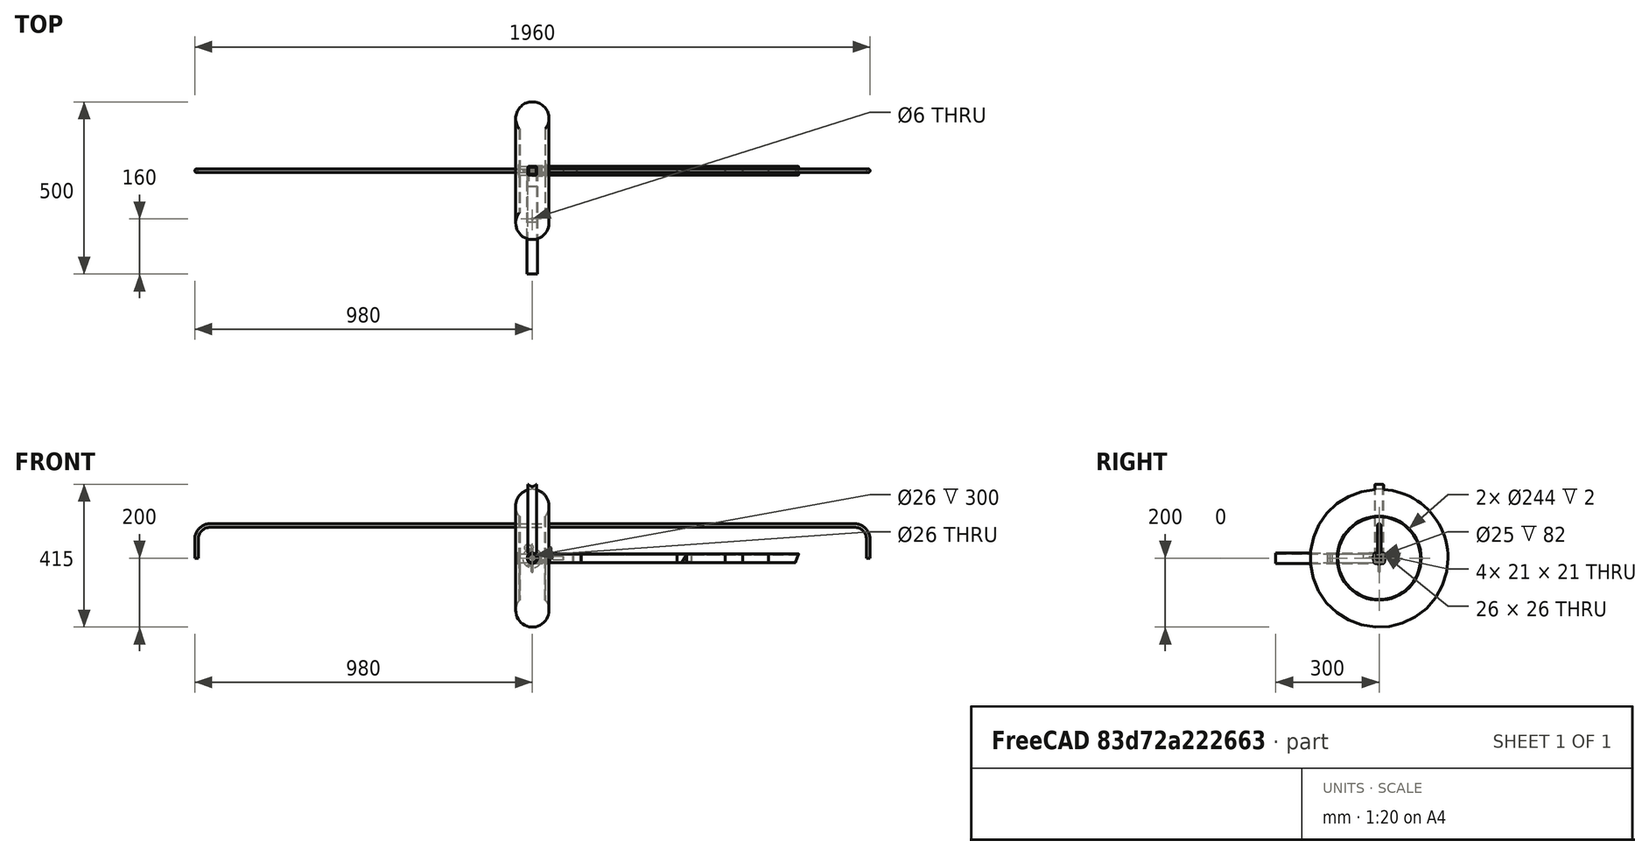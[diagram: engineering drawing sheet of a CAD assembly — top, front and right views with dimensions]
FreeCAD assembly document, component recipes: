
FREECAD ASSEMBLY — COMPONENT RECIPES ("brouetteas4")

This assembly document has 25 components, labeled P0..P24 below (a component is one placed body or linked part). 24 of them carry a construction recipe — the FreeCAD feature program that regenerates the part from scratch, quoted from this document or its linked companion documents; the rest are supplied as boundary geometry only. No exploded tour is included for this assembly.
COMPONENT P0 — recipe-attached ("A1", modeled in this document).
Construction recipe (the document's own serialized feature program — sketch geometry with constraints, then the solid features built on it; lengths are millimeters unless a unit is written):

FEATURE [PartDesign::Body] A1005
  AllowCompound = false
  Origin = -> Origin015
COMPONENT P1 — recipe-attached ("A2", modeled in this document).
Construction recipe (the document's own serialized feature program — sketch geometry with constraints, then the solid features built on it; lengths are millimeters unless a unit is written):

FEATURE [PartDesign::Body] Body001
  AllowCompound = false
  Origin = -> Origin004
COMPONENT P2 — recipe-attached ("A3", modeled in this document).
Construction recipe (the document's own serialized feature program — sketch geometry with constraints, then the solid features built on it; lengths are millimeters unless a unit is written):

FEATURE [Sketcher::SketchObject] Sketch002
  ArcFitTolerance = 0
  AttachmentSupport = -> [XZ_Plane007]
  FullyConstrained = true
  MakeInternals = false
  MapMode = 5
  Placement = pos=(0,0,0) rot=(1,0,0;1.5708rad)
  expr: .Constraints.longueur = Spreadsheet.B4 - Spreadsheet.B2 * 2 - 10
  expr: Constraints[4] = Spreadsheet.B2
  sketch-geometry (7):
    g0: LineSegment StartX=-975 StartY=0 StartZ=0 EndX=-975 EndY=25 EndZ=0
    g1: LineSegment StartX=975 StartY=8e-16 StartZ=0 EndX=975 EndY=25 EndZ=0
    g2: LineSegment StartX=-975 StartY=25 StartZ=0 EndX=-975 EndY=55 EndZ=0
    g3: LineSegment StartX=-935 StartY=95 StartZ=0 EndX=935 EndY=95 EndZ=0
    g4: LineSegment StartX=975 StartY=55 StartZ=0 EndX=975 EndY=25 EndZ=0
    g5: ArcOfCircle CenterX=935 CenterY=55 CenterZ=0 NormalX=0 NormalY=0 NormalZ=1 AngleXU=0 Radius=40 StartAngle=0 EndAngle=1.5708
    g6: ArcOfCircle CenterX=-935 CenterY=55 CenterZ=0 NormalX=0 NormalY=0 NormalZ=1 AngleXU=0 Radius=40 StartAngle=1.5708 EndAngle=3.14159
  constraints (19):
    c: PointOnObject(g0,g-1)
    c: Vertical(g0)
    c: Vertical(g1)
    c: Symmetric(g0,g1,g-2)
    c: DistanceY(g0,g0) = 25
    c: DistanceX(g0,g1) = 1950  'longueur'
    c: Equal(g1,g0)
    c: Coincident(g0,g2)
    c: Vertical(g2)
    c: Horizontal(g3)
    c: Coincident(g4,g1)
    c: Vertical(g4)
    c: Tangent(g3,g5) = 1.5708
    c: Tangent(g4,g5) = 1.5708
    c: Tangent(g2,g6) = 1.5708
    c: Tangent(g3,g6) = 1.5708
    c: Equal(g6,g5)
    c: DistanceY(g0,g3) = 70
    c: Radius(g6) = 40
FEATURE [Sketcher::SketchObject] Sketch003
  ArcFitTolerance = 0
  AttachmentSupport = -> [XY_Plane007]
  ExternalGeometry = -> [Sketch002]
  FullyConstrained = true
  MakeInternals = false
  MapMode = 5
  sketch-geometry (1):
    g0: Circle CenterX=-975 CenterY=0 CenterZ=0 NormalX=0 NormalY=0 NormalZ=1 AngleXU=0 Radius=5
  constraints (2):
    c: Coincident(g0,g-3)
    c: Diameter(g0) = 10
FEATURE [PartDesign::AdditivePipe] AdditivePipe
  AuxilleryCurvelinear = true
  AuxillerySpineTangent = false
  Binormal = (0,0,0)
  Mode = 0
  Profile = -> Sketch003
  Spine = -> Sketch002
  SpineTangent = false
  Suppressed = false
  Transformation = 0
  Transition = 0
FEATURE [PartDesign::Body] Body002
  AllowCompound = false
  Group = -> [Sketch002,Sketch003,AdditivePipe]
  Origin = -> Origin007
  Tip = -> AdditivePipe
COMPONENT P3 — recipe-attached ("A4", modeled in this document).
Construction recipe (the document's own serialized feature program — sketch geometry with constraints, then the solid features built on it; lengths are millimeters unless a unit is written):

FEATURE [Sketcher::SketchObject] Sketch004
  ArcFitTolerance = 0
  AttachmentSupport = -> [YZ_Plane008]
  FullyConstrained = true
  MakeInternals = false
  MapMode = 5
  Placement = pos=(0,0,0) rot=(0.57735,0.57735,0.57735;2.0944rad)
  sketch-geometry (1):
    g0: Circle CenterX=0 CenterY=0 CenterZ=0 NormalX=0 NormalY=0 NormalZ=1 AngleXU=0 Radius=5
  constraints (2):
    c: Coincident(g0,g-1)
    c: Diameter(g0) = 10  'diametre'
FEATURE [PartDesign::Pad] Pad002
  Direction = (1,0,0)
  Length = 90
  Length2 = 100
  Placement = pos=(0,0,0) rot=(0.57735,0.57735,0.57735;2.0944rad)
  Profile = -> Sketch004
  Suppressed = false
  Type = 0
FEATURE [PartDesign::Body] Body003
  AllowCompound = false
  Group = -> [Sketch004,Pad002]
  Origin = -> Origin008
  Tip = -> Pad002
COMPONENT P4 — recipe-attached ("A5", modeled in this document).
Construction recipe (the document's own serialized feature program — sketch geometry with constraints, then the solid features built on it; lengths are millimeters unless a unit is written):

FEATURE [PartDesign::Body] Body005
  AllowCompound = false
  Origin = -> Origin012
COMPONENT P5 — recipe-attached ("A6", modeled in this document).
Construction recipe (the document's own serialized feature program — sketch geometry with constraints, then the solid features built on it; lengths are millimeters unless a unit is written):

FEATURE [Sketcher::SketchObject] Sketch008
  ArcFitTolerance = 0
  FullyConstrained = true
  MakeInternals = false
  MapMode = 2
  Placement = pos=(0,0,0) rot=(0.57735,0.57735,0.57735;2.0944rad)
  expr: Constraints[15] = .Constraints.hauteur * 0.1
  expr: Constraints[27] = .Constraints.epaisseur
  sketch-geometry (12):
    g0: LineSegment StartX=-10 StartY=12.5 StartZ=0 EndX=10 EndY=12.5 EndZ=0
    g1: LineSegment StartX=12.5 StartY=10 StartZ=0 EndX=12.5 EndY=-10 EndZ=0
    g2: LineSegment StartX=10 StartY=-12.5 StartZ=0 EndX=-10 EndY=-12.5 EndZ=0
    g3: LineSegment StartX=-12.5 StartY=-10 StartZ=0 EndX=-12.5 EndY=10 EndZ=0
    g4: ArcOfCircle CenterX=-10 CenterY=10 CenterZ=0 NormalX=0 NormalY=0 NormalZ=1 AngleXU=0 Radius=2.5 StartAngle=1.5708 EndAngle=3.14159
    g5: ArcOfCircle CenterX=10 CenterY=10 CenterZ=0 NormalX=0 NormalY=0 NormalZ=1 AngleXU=0 Radius=2.5 StartAngle=2e-16 EndAngle=1.5708
    g6: ArcOfCircle CenterX=10 CenterY=-10 CenterZ=0 NormalX=0 NormalY=0 NormalZ=1 AngleXU=0 Radius=2.5 StartAngle=4.71239 EndAngle=6.28319
    g7: ArcOfCircle CenterX=-10 CenterY=-10 CenterZ=0 NormalX=0 NormalY=0 NormalZ=1 AngleXU=0 Radius=2.5 StartAngle=3.14159 EndAngle=4.71239
    g8: LineSegment StartX=-10.5 StartY=10.5 StartZ=0 EndX=10.5 EndY=10.5 EndZ=0
    g9: LineSegment StartX=10.5 StartY=10.5 StartZ=0 EndX=10.5 EndY=-10.5 EndZ=0
    g10: LineSegment StartX=10.5 StartY=-10.5 StartZ=0 EndX=-10.5 EndY=-10.5 EndZ=0
    g11: LineSegment StartX=-10.5 StartY=-10.5 StartZ=0 EndX=-10.5 EndY=10.5 EndZ=0
  constraints (28):
    c: Horizontal(g2)
    c: Vertical(g3)
    c: Tangent(g0,g4) = 1.5708
    c: Tangent(g3,g4) = 1.5708
    c: Tangent(g0,g5) = 1.5708
    c: Tangent(g1,g5) = 1.5708
    c: Tangent(g1,g6) = 1.5708
    c: Tangent(g2,g6) = 1.5708
    c: Tangent(g2,g7) = 1.5708
    c: Tangent(g3,g7) = 1.5708
    c: Equal(g4,g5)
    c: DistanceY(g2,g0) = 25  'hauteur'
    c: DistanceX(g3,g1) = 25  'largeur'
    c: Equal(g5,g6)
    c: Equal(g6,g7)
    c: Radius(g7) = 2.5
    c: Symmetric(g1,g1,g-1)
    c: Symmetric(g0,g0,g-2)
    c: Coincident(g8,g9)
    c: Coincident(g9,g10)
    c: Coincident(g10,g11)
    c: Coincident(g11,g8)
    c: Horizontal(g10)
    c: Vertical(g11)
    c: Symmetric(g8,g9,g-1)
    c: Symmetric(g8,g8,g-2)
    c: DistanceX(g3,g8) = 2  'epaisseur'
    c: DistanceY(g2,g9) = 2
FEATURE [PartDesign::Pad] Pad004
  Direction = (1,1e-16,-1e-16)
  Length = 420
  Length2 = 100
  Placement = pos=(0,0,0) rot=(0.57735,0.57735,0.57735;2.0944rad)
  Profile = -> Sketch008
  Suppressed = false
  Type = 0
  expr: Length = Spreadsheet.D4 - Spreadsheet.B9 * 2
FEATURE [PartDesign::Body] Body006
  AllowCompound = false
  Group = -> [Sketch008,Pad004]
  Origin = -> Origin014
  Tip = -> Pad004
COMPONENT P6 — recipe-attached ("A7", modeled in this document).
Construction recipe (the document's own serialized feature program — sketch geometry with constraints, then the solid features built on it; lengths are millimeters unless a unit is written):

FEATURE [PartDesign::Body] A7002
  AllowCompound = false
COMPONENT P7 — recipe-attached ("A8", modeled in this document).
Construction recipe (the document's own serialized feature program — sketch geometry with constraints, then the solid features built on it; lengths are millimeters unless a unit is written):

FEATURE [PartDesign::CoordinateSystem] LCS_0013
  AttacherType = Attacher::AttachEngine3D
  AttachmentSupport = -> [X_Axis020]
  MapMode = 2
FEATURE [PartDesign::Body] A8001
  AllowCompound = false
  Group = -> [LCS_0013]
  Origin = -> Origin018
COMPONENT P8 — recipe-attached ("A9", modeled in this document).
Construction recipe (the document's own serialized feature program — sketch geometry with constraints, then the solid features built on it; lengths are millimeters unless a unit is written):

FEATURE [Sketcher::SketchObject] Sketch011
  ArcFitTolerance = 0
  FullyConstrained = true
  MakeInternals = false
  MapMode = 5
  expr: Constraints[15] = .Constraints.hauteur * 0.1
  expr: Constraints[27] = .Constraints.epaisseur
  sketch-geometry (12):
    g0: LineSegment StartX=-10 StartY=12.5 StartZ=0 EndX=10 EndY=12.5 EndZ=0
    g1: LineSegment StartX=12.5 StartY=10 StartZ=0 EndX=12.5 EndY=-10 EndZ=0
    g2: LineSegment StartX=10 StartY=-12.5 StartZ=0 EndX=-10 EndY=-12.5 EndZ=0
    g3: LineSegment StartX=-12.5 StartY=-10 StartZ=0 EndX=-12.5 EndY=10 EndZ=0
    g4: ArcOfCircle CenterX=-10 CenterY=10 CenterZ=0 NormalX=0 NormalY=0 NormalZ=1 AngleXU=0 Radius=2.5 StartAngle=1.5708 EndAngle=3.14159
    g5: ArcOfCircle CenterX=10 CenterY=10 CenterZ=0 NormalX=0 NormalY=0 NormalZ=1 AngleXU=0 Radius=2.5 StartAngle=2e-16 EndAngle=1.5708
    g6: ArcOfCircle CenterX=10 CenterY=-10 CenterZ=0 NormalX=0 NormalY=0 NormalZ=1 AngleXU=0 Radius=2.5 StartAngle=4.71239 EndAngle=6.28319
    g7: ArcOfCircle CenterX=-10 CenterY=-10 CenterZ=0 NormalX=0 NormalY=0 NormalZ=1 AngleXU=0 Radius=2.5 StartAngle=3.14159 EndAngle=4.71239
    g8: LineSegment StartX=-10.5 StartY=10.5 StartZ=0 EndX=10.5 EndY=10.5 EndZ=0
    g9: LineSegment StartX=10.5 StartY=10.5 StartZ=0 EndX=10.5 EndY=-10.5 EndZ=0
    g10: LineSegment StartX=10.5 StartY=-10.5 StartZ=0 EndX=-10.5 EndY=-10.5 EndZ=0
    g11: LineSegment StartX=-10.5 StartY=-10.5 StartZ=0 EndX=-10.5 EndY=10.5 EndZ=0
  constraints (28):
    c: Horizontal(g2)
    c: Vertical(g3)
    c: Tangent(g0,g4) = 1.5708
    c: Tangent(g3,g4) = 1.5708
    c: Tangent(g0,g5) = 1.5708
    c: Tangent(g1,g5) = 1.5708
    c: Tangent(g1,g6) = 1.5708
    c: Tangent(g2,g6) = 1.5708
    c: Tangent(g2,g7) = 1.5708
    c: Tangent(g3,g7) = 1.5708
    c: Equal(g4,g5)
    c: DistanceY(g2,g0) = 25  'hauteur'
    c: DistanceX(g3,g1) = 25  'largeur'
    c: Equal(g5,g6)
    c: Equal(g6,g7)
    c: Radius(g7) = 2.5
    c: Symmetric(g1,g1,g-1)
    c: Symmetric(g0,g0,g-2)
    c: Coincident(g8,g9)
    c: Coincident(g9,g10)
    c: Coincident(g10,g11)
    c: Coincident(g11,g8)
    c: Horizontal(g10)
    c: Vertical(g11)
    c: Symmetric(g8,g9,g-1)
    c: Symmetric(g8,g8,g-2)
    c: DistanceX(g3,g8) = 2  'epaisseur'
    c: DistanceY(g2,g9) = 2
FEATURE [PartDesign::Pad] Pad007
  Direction = (0,0,1)
  Length = 215
  Length2 = 100
  Profile = -> Sketch011
  Suppressed = false
  Type = 0
  expr: Length = Spreadsheet.B11 - Spreadsheet.B5 - Spreadsheet.B2 * 2
FEATURE [PartDesign::CoordinateSystem] LCS_0014
  AttacherType = Attacher::AttachEngine3D
  AttachmentSupport = -> [X_Axis021]
  MapMode = 2
FEATURE [Sketcher::SketchObject] Sketch023
  ArcFitTolerance = 0
  AttachmentSupport = -> [Pad007]
  ExternalGeometry = -> [Pad007]
  FullyConstrained = true
  MakeInternals = false
  MapMode = 5
  Placement = pos=(0,-12.5,0) rot=(1,0,0;1.5708rad)
  expr: Constraints[0] = Spreadsheet.B13
  sketch-geometry (1):
    g0: Circle CenterX=0 CenterY=223.292 CenterZ=0 NormalX=0 NormalY=0 NormalZ=1 AngleXU=0 Radius=15
  constraints (4):
    c: Diameter(g0) = 30
    c: PointOnObject(g0,g-2)
    c: PointOnObject(g-4,g0)
    c: DistanceY(g-4,g0) = 8.29156  'deport'
FEATURE [PartDesign::Pocket] Pocket
  BaseFeature = -> Pad007
  Direction = (0,1,-2e-16)
  Length = 5
  Length2 = 100
  Profile = -> Sketch023
  Suppressed = false
  Type = 1
FEATURE [PartDesign::Body] A8004
  AllowCompound = false
  Group = -> [LCS_0014,Pad007,Sketch011,Sketch023,Pocket]
  Origin = -> Origin020
  Tip = -> Pocket
COMPONENT P9 — geometry summary ("Model"; no construction recipe available for this part):
  bounding box: 2615.0 x 1135.0 x 687.0 mm
  tessellated surface: 70,444 triangles
  volume: 24691210 mm^3 (1% of its bounding box)
  symmetry: mirror-symmetric across its y mid-plane
COMPONENT P10 — recipe-attached ("A10", modeled in this document).
Construction recipe (the document's own serialized feature program — sketch geometry with constraints, then the solid features built on it; lengths are millimeters unless a unit is written):

FEATURE [Sketcher::SketchObject] Sketch012
  ArcFitTolerance = 0
  AttachmentSupport = -> [XZ_Plane022]
  FullyConstrained = true
  MakeInternals = false
  MapMode = 5
  Placement = pos=(0,0,0) rot=(1,0,0;1.5708rad)
  sketch-geometry (1):
    g0: Circle CenterX=0 CenterY=0 CenterZ=0 NormalX=0 NormalY=0 NormalZ=1 AngleXU=0 Radius=12.5
  constraints (2):
    c: Coincident(g0,g-1)
    c: Diameter(g0) = 25  'diametre'
FEATURE [PartDesign::Pad] Pad008
  Direction = (0,-1,2e-16)
  Length = 150
  Length2 = 100
  Placement = pos=(0,0,0) rot=(1,0,0;1.5708rad)
  Profile = -> Sketch012
  Suppressed = false
  Type = 0
FEATURE [PartDesign::Plane] DatumPlane004
  AttachmentOffset = pos=(0,0,12.5) rot=(0,0,1;0rad)
  AttachmentSupport = -> [XY_Plane022]
  Length = 60
  MapMode = 5
  Placement = pos=(0,0,12.5) rot=(0,0,1;0rad)
  ResizeMode = 0
  Width = 60
FEATURE [Sketcher::SketchObject] Sketch034
  ArcFitTolerance = 1e-06
  AttachmentSupport = -> [DatumPlane004]
  FullyConstrained = false
  MakeInternals = false
  MapMode = 5
  Placement = pos=(0,0,12.5) rot=(0,0,1;0rad)
  expr: Constraints[0] = Pad008.Length - 10 mm
  sketch-geometry (1):
    g0: Circle CenterX=0 CenterY=-140 CenterZ=0 NormalX=0 NormalY=0 NormalZ=1 AngleXU=0 Radius=16.367
  constraints (2):
    c: DistanceY(g0,g-1) = 140
    c: PointOnObject(g0,g-2)
FEATURE [PartDesign::Hole] Hole
  BaseFeature = -> Pad008
  CustomThreadClearance = 0
  Depth = 326.607
  DepthType = 1
  Diameter = 6
  DrillForDepth = false
  DrillPoint = 1
  DrillPointAngle = 118
  HoleCutCountersinkAngle = 90
  HoleCutCustomValues = false
  HoleCutDepth = 0
  HoleCutDiameter = 6.1
  HoleCutType = 0
  ModelThread = false
  Placement = pos=(0,0,0) rot=(1,0,0;1.5708rad)
  Profile = -> Sketch034
  Suppressed = false
  Tapered = false
  TaperedAngle = 90
  ThreadClass = 0
  ThreadDepth = 326.607
  ThreadDepthType = 0
  ThreadDirection = 0
  ThreadFit = 0
  ThreadSize = 0
  ThreadType = 0
  Threaded = false
  UseCustomThreadClearance = false
FEATURE [PartDesign::Body] Body
  AllowCompound = false
  Group = -> [Sketch012,Pad008,Sketch034,DatumPlane004,Hole]
  Origin = -> Origin022
  Tip = -> Hole
COMPONENT P11 — recipe-attached ("A11", modeled in this document).
Construction recipe (the document's own serialized feature program — sketch geometry with constraints, then the solid features built on it; lengths are millimeters unless a unit is written):

FEATURE [Sketcher::SketchObject] Sketch013
  ArcFitTolerance = 0
  AttachmentSupport = -> [XZ_Plane024]
  FullyConstrained = true
  MakeInternals = false
  MapMode = 5
  Placement = pos=(0,0,0) rot=(1,0,0;1.5708rad)
  expr: Constraints[22] = .Constraints.epaisseur
  expr: Constraints[24] = .Constraints.largeur * 20 / 100
  sketch-geometry (10):
    g0: LineSegment StartX=-15 StartY=15 StartZ=0 EndX=-15 EndY=0 EndZ=0
    g1: LineSegment StartX=-15 StartY=0 StartZ=0 EndX=15 EndY=0 EndZ=0
    g2: LineSegment StartX=15 StartY=0 StartZ=0 EndX=15 EndY=15 EndZ=0
    g3: LineSegment StartX=15 StartY=15 StartZ=0 EndX=14 EndY=15 EndZ=0
    g4: LineSegment StartX=11 StartY=12 StartZ=0 EndX=11 EndY=4 EndZ=0
    g5: LineSegment StartX=11 StartY=4 StartZ=0 EndX=-11 EndY=4 EndZ=0
    g6: LineSegment StartX=-11 StartY=4 StartZ=0 EndX=-11 EndY=12 EndZ=0
    g7: LineSegment StartX=-14 StartY=15 StartZ=0 EndX=-15 EndY=15 EndZ=0
    g8: ArcOfCircle CenterX=-14 CenterY=12 CenterZ=0 NormalX=0 NormalY=0 NormalZ=1 AngleXU=0 Radius=3 StartAngle=0 EndAngle=1.5708
    g9: ArcOfCircle CenterX=14 CenterY=12 CenterZ=0 NormalX=0 NormalY=0 NormalZ=1 AngleXU=0 Radius=3 StartAngle=1.5708 EndAngle=3.14159
  constraints (25):
    c: PointOnObject(g0,g-1)
    c: Vertical(g0)
    c: Coincident(g0,g1)
    c: Coincident(g1,g2)
    c: Coincident(g2,g3)
    c: Horizontal(g3)
    c: Vertical(g4)
    c: Coincident(g4,g5)
    c: Coincident(g5,g6)
    c: Coincident(g7,g0)
    c: Horizontal(g7)
    c: Symmetric(g1,g0,g-2)
    c: Symmetric(g5,g4,g-2)
    c: Tangent(g6,g8) = -1.5708
    c: Tangent(g7,g8) = -1.5708
    c: Tangent(g3,g9) = -1.5708
    c: Tangent(g4,g9) = -1.5708
    c: Equal(g8,g9)
    c: Symmetric(g0,g2,g-2)
    c: Vertical(g6)
    c: DistanceX(g1,g1) = 30  'largeur'
    c: DistanceY(g2,g2) = 15  'hauteur'
    c: DistanceY(g1,g4) = 4
    c: DistanceX(g4,g1) = 4  'epaisseur'
    c: Diameter(g8) = 6
FEATURE [PartDesign::Pad] Pad009
  Direction = (0,-1,2e-16)
  Length = 46
  Length2 = 100
  Placement = pos=(0,0,0) rot=(1,0,0;1.5708rad)
  Profile = -> Sketch013
  Suppressed = false
  Type = 0
FEATURE [PartDesign::Body] Body007
  AllowCompound = false
  Group = -> [Sketch013,Pad009]
  Origin = -> Origin024
  Tip = -> Pad009
COMPONENT P12 — recipe-attached ("A12", modeled in this document).
Construction recipe (the document's own serialized feature program — sketch geometry with constraints, then the solid features built on it; lengths are millimeters unless a unit is written):

FEATURE [PartDesign::Body] Body008
  AllowCompound = false
  Origin = -> Origin028
COMPONENT P13 — recipe-attached ("A13", modeled in this document).
Construction recipe (the document's own serialized feature program — sketch geometry with constraints, then the solid features built on it; lengths are millimeters unless a unit is written):

FEATURE [Sketcher::SketchObject] Sketch016
  ArcFitTolerance = 0
  FullyConstrained = true
  MakeInternals = false
  MapMode = 5
  Placement = pos=(0,0,0) rot=(0.57735,0.57735,0.57735;2.0944rad)
  expr: Constraints[15] = .Constraints.hauteur * 0.1
  expr: Constraints[27] = .Constraints.epaisseur
  sketch-geometry (12):
    g0: LineSegment StartX=-10 StartY=12.5 StartZ=0 EndX=10 EndY=12.5 EndZ=0
    g1: LineSegment StartX=12.5 StartY=10 StartZ=0 EndX=12.5 EndY=-10 EndZ=0
    g2: LineSegment StartX=10 StartY=-12.5 StartZ=0 EndX=-10 EndY=-12.5 EndZ=0
    g3: LineSegment StartX=-12.5 StartY=-10 StartZ=0 EndX=-12.5 EndY=10 EndZ=0
    g4: ArcOfCircle CenterX=-10 CenterY=10 CenterZ=0 NormalX=0 NormalY=0 NormalZ=1 AngleXU=0 Radius=2.5 StartAngle=1.5708 EndAngle=3.14159
    g5: ArcOfCircle CenterX=10 CenterY=10 CenterZ=0 NormalX=0 NormalY=0 NormalZ=1 AngleXU=0 Radius=2.5 StartAngle=2e-16 EndAngle=1.5708
    g6: ArcOfCircle CenterX=10 CenterY=-10 CenterZ=0 NormalX=0 NormalY=0 NormalZ=1 AngleXU=0 Radius=2.5 StartAngle=4.71239 EndAngle=6.28319
    g7: ArcOfCircle CenterX=-10 CenterY=-10 CenterZ=0 NormalX=0 NormalY=0 NormalZ=1 AngleXU=0 Radius=2.5 StartAngle=3.14159 EndAngle=4.71239
    g8: LineSegment StartX=-10.5 StartY=10.5 StartZ=0 EndX=10.5 EndY=10.5 EndZ=0
    g9: LineSegment StartX=10.5 StartY=10.5 StartZ=0 EndX=10.5 EndY=-10.5 EndZ=0
    g10: LineSegment StartX=10.5 StartY=-10.5 StartZ=0 EndX=-10.5 EndY=-10.5 EndZ=0
    g11: LineSegment StartX=-10.5 StartY=-10.5 StartZ=0 EndX=-10.5 EndY=10.5 EndZ=0
  constraints (28):
    c: Horizontal(g2)
    c: Vertical(g3)
    c: Tangent(g0,g4) = 1.5708
    c: Tangent(g3,g4) = 1.5708
    c: Tangent(g0,g5) = 1.5708
    c: Tangent(g1,g5) = 1.5708
    c: Tangent(g1,g6) = 1.5708
    c: Tangent(g2,g6) = 1.5708
    c: Tangent(g2,g7) = 1.5708
    c: Tangent(g3,g7) = 1.5708
    c: Equal(g4,g5)
    c: DistanceY(g2,g0) = 25  'hauteur'
    c: DistanceX(g3,g1) = 25  'largeur'
    c: Equal(g5,g6)
    c: Equal(g6,g7)
    c: Radius(g7) = 2.5
    c: Symmetric(g1,g1,g-1)
    c: Symmetric(g0,g0,g-2)
    c: Coincident(g8,g9)
    c: Coincident(g9,g10)
    c: Coincident(g10,g11)
    c: Coincident(g11,g8)
    c: Horizontal(g10)
    c: Vertical(g11)
    c: Symmetric(g8,g9,g-1)
    c: Symmetric(g8,g8,g-2)
    c: DistanceX(g3,g8) = 2  'epaisseur'
    c: DistanceY(g2,g9) = 2
FEATURE [PartDesign::Pad] Pad011
  Direction = (1,1e-16,-1e-16)
  Length = 449.646
  Length2 = 100
  Placement = pos=(0,0,0) rot=(0.57735,0.57735,0.57735;2.0944rad)
  Profile = -> Sketch016
  Suppressed = false
  Type = 0
  expr: Length = Sketch014.Constraints.lpied
FEATURE [Sketcher::SketchObject] Sketch028
  ArcFitTolerance = 1e-06
  AttachmentSupport = -> [YZ_Plane029]
  ExternalGeometry = -> [Pad011]
  FullyConstrained = false
  MakeInternals = false
  MapMode = 5
  Placement = pos=(0,0,0) rot=(0.57735,0.57735,0.57735;2.0944rad)
  sketch-geometry (5):
    g0: LineSegment StartX=-17.5 StartY=12.5 StartZ=0 EndX=-17.5 EndY=-57.5 EndZ=0
    g1: LineSegment StartX=-17.5 StartY=-57.5 StartZ=0 EndX=17.5 EndY=-57.5 EndZ=0
    g2: LineSegment StartX=17.5 StartY=-57.5 StartZ=0 EndX=17.5 EndY=12.5 EndZ=0
    g3: LineSegment StartX=17.5 StartY=12.5 StartZ=0 EndX=-17.5 EndY=12.5 EndZ=0
    g4: LineSegment [constr] StartX=-59.8857 StartY=12.5 StartZ=0 EndX=133.957 EndY=12.5 EndZ=0
  constraints (13):
    c: Coincident(g0,g1)
    c: Coincident(g1,g2)
    c: Coincident(g2,g3)
    c: Coincident(g3,g0)
    c: Vertical(g0)
    c: Vertical(g2)
    c: Horizontal(g1)
    c: Horizontal(g4)
    c: PointOnObject(g2,g4)
    c: DistanceX(g1,g1) = 35
    c: DistanceY(g2,g2) = 70
    c: Symmetric(g0,g2,g-2)
    c: PointOnObject(g-3,g4)
FEATURE [PartDesign::Groove] Groove002
  Angle = 56.5107
  Angle2 = 60
  Axis = (0,193.843,0)
  Base = (0,-59.8857,12.5)
  BaseFeature = -> Pad011
  Placement = pos=(0,0,0) rot=(0.57735,0.57735,0.57735;2.0944rad)
  Profile = -> Sketch028
  ReferenceAxis = -> Sketch028 [Axis]
  Reversed = true
  Suppressed = false
  Type = 0
  expr: Angle = 90 ° - Sketch014.Constraints.angle
FEATURE [PartDesign::Plane] DatumPlane001
  AttachmentSupport = -> [Groove002]
  Length = 60
  MapMode = 5
  Placement = pos=(449.646,1.978e-13,0) rot=(0.57735,0.57735,0.57735;2.0944rad)
  ResizeMode = 0
  Width = 60
FEATURE [Sketcher::SketchObject] Sketch029
  ArcFitTolerance = 1e-06
  AttachmentSupport = -> [DatumPlane001]
  ExternalGeometry = -> [Groove002]
  FullyConstrained = false
  MakeInternals = false
  MapMode = 5
  Placement = pos=(449.646,1.978e-13,0) rot=(0.57735,0.57735,0.57735;2.0944rad)
  sketch-geometry (5):
    g0: LineSegment [constr] StartX=-50.285 StartY=12.5 StartZ=0 EndX=61.7161 EndY=12.5 EndZ=0
    g1: LineSegment StartX=-17.5 StartY=12.5 StartZ=0 EndX=-17.5 EndY=-57.5 EndZ=0
    g2: LineSegment StartX=-17.5 StartY=-57.5 StartZ=0 EndX=17.5 EndY=-57.5 EndZ=0
    g3: LineSegment StartX=17.5 StartY=-57.5 StartZ=0 EndX=17.5 EndY=12.5 EndZ=0
    g4: LineSegment StartX=17.5 StartY=12.5 StartZ=0 EndX=-17.5 EndY=12.5 EndZ=0
  constraints (13):
    c: Horizontal(g0)
    c: PointOnObject(g-3,g0)
    c: Coincident(g1,g2)
    c: Coincident(g2,g3)
    c: Coincident(g3,g4)
    c: Coincident(g4,g1)
    c: Vertical(g1)
    c: Vertical(g3)
    c: Horizontal(g2)
    c: Distance(g1,g3) = 35
    c: Distance(g2,g4) = 70
    c: PointOnObject(g1,g0)
    c: Symmetric(g3,g1,g-2)
FEATURE [PartDesign::Groove] Groove003
  Angle = 33.4893
  Angle2 = 60
  Axis = (-1.492e-13,112.001,0)
  Base = (449.646,-50.285,12.5)
  BaseFeature = -> Groove002
  Placement = pos=(0,0,0) rot=(0.57735,0.57735,0.57735;2.0944rad)
  Profile = -> Sketch029
  ReferenceAxis = -> Sketch029 [Axis]
  Suppressed = false
  Type = 0
  expr: Angle = Sketch014.Constraints.angle
FEATURE [PartDesign::Body] Body009
  AllowCompound = false
  Group = -> [Sketch016,Pad011,Sketch028,Groove002,DatumPlane001,Sketch029,Groove003]
  Origin = -> Origin029
  Tip = -> Groove003
COMPONENT P14 — recipe-attached ("A14", modeled in this document).
Construction recipe (the document's own serialized feature program — sketch geometry with constraints, then the solid features built on it; lengths are millimeters unless a unit is written):

FEATURE [Sketcher::SketchObject] Sketch017
  ArcFitTolerance = 0
  FullyConstrained = true
  MakeInternals = false
  MapMode = 5
  Placement = pos=(0,0,0) rot=(0.57735,0.57735,0.57735;2.0944rad)
  expr: Constraints[15] = .Constraints.hauteur * 0.1
  expr: Constraints[27] = .Constraints.epaisseur
  sketch-geometry (12):
    g0: LineSegment StartX=-10 StartY=12.5 StartZ=0 EndX=10 EndY=12.5 EndZ=0
    g1: LineSegment StartX=12.5 StartY=10 StartZ=0 EndX=12.5 EndY=-10 EndZ=0
    g2: LineSegment StartX=10 StartY=-12.5 StartZ=0 EndX=-10 EndY=-12.5 EndZ=0
    g3: LineSegment StartX=-12.5 StartY=-10 StartZ=0 EndX=-12.5 EndY=10 EndZ=0
    g4: ArcOfCircle CenterX=-10 CenterY=10 CenterZ=0 NormalX=0 NormalY=0 NormalZ=1 AngleXU=0 Radius=2.5 StartAngle=1.5708 EndAngle=3.14159
    g5: ArcOfCircle CenterX=10 CenterY=10 CenterZ=0 NormalX=0 NormalY=0 NormalZ=1 AngleXU=0 Radius=2.5 StartAngle=2e-16 EndAngle=1.5708
    g6: ArcOfCircle CenterX=10 CenterY=-10 CenterZ=0 NormalX=0 NormalY=0 NormalZ=1 AngleXU=0 Radius=2.5 StartAngle=4.71239 EndAngle=6.28319
    g7: ArcOfCircle CenterX=-10 CenterY=-10 CenterZ=0 NormalX=0 NormalY=0 NormalZ=1 AngleXU=0 Radius=2.5 StartAngle=3.14159 EndAngle=4.71239
    g8: LineSegment StartX=-10.5 StartY=10.5 StartZ=0 EndX=10.5 EndY=10.5 EndZ=0
    g9: LineSegment StartX=10.5 StartY=10.5 StartZ=0 EndX=10.5 EndY=-10.5 EndZ=0
    g10: LineSegment StartX=10.5 StartY=-10.5 StartZ=0 EndX=-10.5 EndY=-10.5 EndZ=0
    g11: LineSegment StartX=-10.5 StartY=-10.5 StartZ=0 EndX=-10.5 EndY=10.5 EndZ=0
  constraints (28):
    c: Horizontal(g2)
    c: Vertical(g3)
    c: Tangent(g0,g4) = 1.5708
    c: Tangent(g3,g4) = 1.5708
    c: Tangent(g0,g5) = 1.5708
    c: Tangent(g1,g5) = 1.5708
    c: Tangent(g1,g6) = 1.5708
    c: Tangent(g2,g6) = 1.5708
    c: Tangent(g2,g7) = 1.5708
    c: Tangent(g3,g7) = 1.5708
    c: Equal(g4,g5)
    c: DistanceY(g2,g0) = 25  'hauteur'
    c: DistanceX(g3,g1) = 25  'largeur'
    c: Equal(g5,g6)
    c: Equal(g6,g7)
    c: Radius(g7) = 2.5
    c: Symmetric(g1,g1,g-1)
    c: Symmetric(g0,g0,g-2)
    c: Coincident(g8,g9)
    c: Coincident(g9,g10)
    c: Coincident(g10,g11)
    c: Coincident(g11,g8)
    c: Horizontal(g10)
    c: Vertical(g11)
    c: Symmetric(g8,g9,g-1)
    c: Symmetric(g8,g8,g-2)
    c: DistanceX(g3,g8) = 2  'epaisseur'
    c: DistanceY(g2,g9) = 2
FEATURE [PartDesign::Pad] Pad012
  Direction = (1,1e-16,-1e-16)
  Length = 772.835
  Length2 = 100
  Placement = pos=(0,0,0) rot=(0.57735,0.57735,0.57735;2.0944rad)
  Profile = -> Sketch017
  ReferenceAxis = -> Sketch017 [N_Axis]
  Suppressed = false
  Type = 0
  expr: Length = Sketch014.Constraints.ldiag + Sketch014.Constraints.rajoueroue
FEATURE [Sketcher::SketchObject] Sketch032
  ArcFitTolerance = 1e-06
  AttachmentSupport = -> [YZ_Plane030]
  ExternalGeometry = -> [Pad012]
  FullyConstrained = false
  MakeInternals = false
  MapMode = 5
  Placement = pos=(0,0,0) rot=(0.57735,0.57735,0.57735;2.0944rad)
  sketch-geometry (5):
    g0: LineSegment StartX=17.5 StartY=57.5 StartZ=0 EndX=-17.5 EndY=57.5 EndZ=0
    g1: LineSegment StartX=-17.5 StartY=57.5 StartZ=0 EndX=-17.5 EndY=-12.5 EndZ=0
    g2: LineSegment StartX=-17.5 StartY=-12.5 StartZ=0 EndX=17.5 EndY=-12.5 EndZ=0
    g3: LineSegment StartX=17.5 StartY=-12.5 StartZ=0 EndX=17.5 EndY=57.5 EndZ=0
    g4: LineSegment [constr] StartX=69.7742 StartY=-12.5 StartZ=0 EndX=-82.9271 EndY=-12.5 EndZ=0
  constraints (13):
    c: Coincident(g0,g1)
    c: Coincident(g1,g2)
    c: Coincident(g2,g3)
    c: Coincident(g3,g0)
    c: Horizontal(g0)
    c: Vertical(g1)
    c: Vertical(g3)
    c: Distance(g1,g3) = 35
    c: Distance(g0,g2) = 70
    c: Symmetric(g1,g2,g-2)
    c: PointOnObject(g1,g-3)
    c: Horizontal(g4)
    c: PointOnObject(g2,g4)
FEATURE [PartDesign::Groove] Groove006
  Angle = 19.6557
  Angle2 = 60
  Axis = (0,-152.701,0)
  Base = (0,69.7742,-12.5)
  BaseFeature = -> Pad012
  Placement = pos=(0,0,0) rot=(0.57735,0.57735,0.57735;2.0944rad)
  Profile = -> Sketch032
  ReferenceAxis = -> Sketch032 [Axis]
  Reversed = true
  Suppressed = false
  Type = 0
  expr: Angle = 90 ° - Sketch014.Constraints.anglerou
FEATURE [PartDesign::Plane] DatumPlane003
  AttachmentSupport = -> [Groove006]
  Length = 60
  MapMode = 5
  Placement = pos=(772.835,3.4e-13,0) rot=(0.57735,0.57735,0.57735;2.0944rad)
  ResizeMode = 0
  Width = 60
FEATURE [Sketcher::SketchObject] Sketch033
  ArcFitTolerance = 1e-06
  AttachmentSupport = -> [DatumPlane003]
  ExternalGeometry = -> [Groove006]
  FullyConstrained = false
  MakeInternals = false
  MapMode = 5
  Placement = pos=(772.835,3.4e-13,0) rot=(0.57735,0.57735,0.57735;2.0944rad)
  sketch-geometry (5):
    g0: LineSegment [constr] StartX=-118.894 StartY=12.5 StartZ=0 EndX=112.379 EndY=12.5 EndZ=0
    g1: LineSegment StartX=-17.5 StartY=12.5 StartZ=0 EndX=-17.5 EndY=-57.5 EndZ=0
    g2: LineSegment StartX=-17.5 StartY=-57.5 StartZ=0 EndX=17.5 EndY=-57.5 EndZ=0
    g3: LineSegment StartX=17.5 StartY=-57.5 StartZ=0 EndX=17.5 EndY=12.5 EndZ=0
    g4: LineSegment StartX=17.5 StartY=12.5 StartZ=0 EndX=-17.5 EndY=12.5 EndZ=0
  constraints (13):
    c: Horizontal(g0)
    c: Coincident(g1,g2)
    c: Coincident(g2,g3)
    c: Coincident(g3,g4)
    c: Coincident(g4,g1)
    c: Vertical(g1)
    c: Vertical(g3)
    c: Horizontal(g2)
    c: Distance(g1,g3) = 35
    c: Distance(g2,g4) = 70
    c: PointOnObject(g1,g0)
    c: Symmetric(g3,g1,g-2)
    c: PointOnObject(g-3,g0)
FEATURE [PartDesign::Groove] Groove007
  Angle = 19.66
  Angle2 = 60
  Axis = (-3.081e-13,231.273,0)
  Base = (772.835,-118.894,12.5)
  BaseFeature = -> Groove006
  Placement = pos=(0,0,0) rot=(0.57735,0.57735,0.57735;2.0944rad)
  Profile = -> Sketch033
  ReferenceAxis = -> Sketch033 [Axis]
  Suppressed = false
  Type = 0
FEATURE [PartDesign::Body] Body010
  AllowCompound = false
  Group = -> [Sketch017,Pad012,Sketch032,Groove006,DatumPlane003,Sketch033,Groove007]
  Origin = -> Origin030
  Tip = -> Groove007
COMPONENT P15 — recipe-attached ("A15", modeled in this document).
Construction recipe (the document's own serialized feature program — sketch geometry with constraints, then the solid features built on it; lengths are millimeters unless a unit is written):

FEATURE [Sketcher::SketchObject] Sketch018
  ArcFitTolerance = 0
  FullyConstrained = true
  MakeInternals = false
  MapMode = 5
  Placement = pos=(0,0,0) rot=(0.57735,0.57735,0.57735;2.0944rad)
  expr: Constraints[15] = .Constraints.hauteur * 0.1
  expr: Constraints[27] = .Constraints.epaisseur
  sketch-geometry (12):
    g0: LineSegment StartX=-10 StartY=12.5 StartZ=0 EndX=10 EndY=12.5 EndZ=0
    g1: LineSegment StartX=12.5 StartY=10 StartZ=0 EndX=12.5 EndY=-10 EndZ=0
    g2: LineSegment StartX=10 StartY=-12.5 StartZ=0 EndX=-10 EndY=-12.5 EndZ=0
    g3: LineSegment StartX=-12.5 StartY=-10 StartZ=0 EndX=-12.5 EndY=10 EndZ=0
    g4: ArcOfCircle CenterX=-10 CenterY=10 CenterZ=0 NormalX=0 NormalY=0 NormalZ=1 AngleXU=0 Radius=2.5 StartAngle=1.5708 EndAngle=3.14159
    g5: ArcOfCircle CenterX=10 CenterY=10 CenterZ=0 NormalX=0 NormalY=0 NormalZ=1 AngleXU=0 Radius=2.5 StartAngle=2e-16 EndAngle=1.5708
    g6: ArcOfCircle CenterX=10 CenterY=-10 CenterZ=0 NormalX=0 NormalY=0 NormalZ=1 AngleXU=0 Radius=2.5 StartAngle=4.71239 EndAngle=6.28319
    g7: ArcOfCircle CenterX=-10 CenterY=-10 CenterZ=0 NormalX=0 NormalY=0 NormalZ=1 AngleXU=0 Radius=2.5 StartAngle=3.14159 EndAngle=4.71239
    g8: LineSegment StartX=-10.5 StartY=10.5 StartZ=0 EndX=10.5 EndY=10.5 EndZ=0
    g9: LineSegment StartX=10.5 StartY=10.5 StartZ=0 EndX=10.5 EndY=-10.5 EndZ=0
    g10: LineSegment StartX=10.5 StartY=-10.5 StartZ=0 EndX=-10.5 EndY=-10.5 EndZ=0
    g11: LineSegment StartX=-10.5 StartY=-10.5 StartZ=0 EndX=-10.5 EndY=10.5 EndZ=0
  constraints (28):
    c: Horizontal(g2)
    c: Vertical(g3)
    c: Tangent(g0,g4) = 1.5708
    c: Tangent(g3,g4) = 1.5708
    c: Tangent(g0,g5) = 1.5708
    c: Tangent(g1,g5) = 1.5708
    c: Tangent(g1,g6) = 1.5708
    c: Tangent(g2,g6) = 1.5708
    c: Tangent(g2,g7) = 1.5708
    c: Tangent(g3,g7) = 1.5708
    c: Equal(g4,g5)
    c: DistanceY(g2,g0) = 25  'hauteur'
    c: DistanceX(g3,g1) = 25  'largeur'
    c: Equal(g5,g6)
    c: Equal(g6,g7)
    c: Radius(g7) = 2.5
    c: Symmetric(g1,g1,g-1)
    c: Symmetric(g0,g0,g-2)
    c: Coincident(g8,g9)
    c: Coincident(g9,g10)
    c: Coincident(g10,g11)
    c: Coincident(g11,g8)
    c: Horizontal(g10)
    c: Vertical(g11)
    c: Symmetric(g8,g9,g-1)
    c: Symmetric(g8,g8,g-2)
    c: DistanceX(g3,g8) = 2  'epaisseur'
    c: DistanceY(g2,g9) = 2
FEATURE [PartDesign::Pad] Pad013
  Direction = (1,1e-16,-1e-16)
  Length = 462
  Length2 = 100
  Placement = pos=(0,0,0) rot=(0.57735,0.57735,0.57735;2.0944rad)
  Profile = -> Sketch018
  Suppressed = false
  Type = 0
  expr: Length = Sketch014.Constraints.l2pied
FEATURE [Sketcher::SketchObject] Sketch030
  ArcFitTolerance = 1e-06
  AttachmentSupport = -> [YZ_Plane032]
  ExternalGeometry = -> [Pad013]
  FullyConstrained = false
  MakeInternals = false
  MapMode = 5
  Placement = pos=(0,0,0) rot=(0.57735,0.57735,0.57735;2.0944rad)
  sketch-geometry (5):
    g0: LineSegment StartX=12.5 StartY=17.5 StartZ=0 EndX=-57.5 EndY=17.5 EndZ=0
    g1: LineSegment StartX=-57.5 StartY=17.5 StartZ=0 EndX=-57.5 EndY=-17.5 EndZ=0
    g2: LineSegment StartX=-57.5 StartY=-17.5 StartZ=0 EndX=12.5 EndY=-17.5 EndZ=0
    g3: LineSegment StartX=12.5 StartY=-17.5 StartZ=0 EndX=12.5 EndY=17.5 EndZ=0
    g4: LineSegment [constr] StartX=12.5 StartY=37.849 StartZ=0 EndX=12.5 EndY=-63.3268 EndZ=0
  constraints (13):
    c: Coincident(g0,g1)
    c: Coincident(g1,g2)
    c: Coincident(g2,g3)
    c: Coincident(g3,g0)
    c: Horizontal(g0)
    c: Vertical(g3)
    c: Distance(g1,g3) = 70
    c: Distance(g0,g2) = 35
    c: Horizontal(g2)
    c: Symmetric(g0,g1,g-1)
    c: Vertical(g4)
    c: PointOnObject(g-3,g4)
    c: PointOnObject(g2,g4)
FEATURE [PartDesign::Groove] Groove004
  Angle = 59.9743
  Angle2 = 60
  Axis = (0,0,-101.176)
  Base = (0,12.5,37.849)
  BaseFeature = -> Pad013
  Placement = pos=(0,0,0) rot=(0.57735,0.57735,0.57735;2.0944rad)
  Profile = -> Sketch030
  ReferenceAxis = -> Sketch030 [Axis]
  Reversed = true
  Suppressed = false
  Type = 0
  expr: Angle = 90 ° - Sketch014.Constraints.angle2
FEATURE [PartDesign::Plane] DatumPlane002
  AttachmentSupport = -> [Groove004]
  Length = 60
  MapMode = 5
  Placement = pos=(462,2.033e-13,0) rot=(0.57735,0.57735,0.57735;2.0944rad)
  ResizeMode = 0
  Width = 60
FEATURE [Sketcher::SketchObject] Sketch031
  ArcFitTolerance = 1e-06
  AttachmentSupport = -> [DatumPlane002]
  ExternalGeometry = -> [Groove004]
  FullyConstrained = false
  MakeInternals = false
  MapMode = 5
  Placement = pos=(462,2.033e-13,0) rot=(0.57735,0.57735,0.57735;2.0944rad)
  sketch-geometry (5):
    g0: LineSegment [constr] StartX=12.5 StartY=67.6644 StartZ=0 EndX=12.5 EndY=-52.0571 EndZ=0
    g1: LineSegment StartX=-57.5 StartY=17.5 StartZ=0 EndX=-57.5 EndY=-17.5 EndZ=0
    g2: LineSegment StartX=-57.5 StartY=-17.5 StartZ=0 EndX=12.5 EndY=-17.5 EndZ=0
    g3: LineSegment StartX=12.5 StartY=-17.5 StartZ=0 EndX=12.5 EndY=17.5 EndZ=0
    g4: LineSegment StartX=12.5 StartY=17.5 StartZ=0 EndX=-57.5 EndY=17.5 EndZ=0
  constraints (13):
    c: Vertical(g0)
    c: Coincident(g1,g2)
    c: Coincident(g2,g3)
    c: Coincident(g3,g4)
    c: Coincident(g4,g1)
    c: Vertical(g3)
    c: Horizontal(g2)
    c: Horizontal(g4)
    c: Distance(g1,g3) = 70
    c: Distance(g2,g4) = 35
    c: PointOnObject(g3,g-3)
    c: PointOnObject(g0,g-3)
    c: Symmetric(g1,g1,g-1)
FEATURE [PartDesign::Groove] Groove005
  Angle = 30.0257
  Angle2 = 60
  Axis = (0,0,-119.722)
  Base = (462,12.5,67.6644)
  BaseFeature = -> Groove004
  Placement = pos=(0,0,0) rot=(0.57735,0.57735,0.57735;2.0944rad)
  Profile = -> Sketch031
  ReferenceAxis = -> Sketch031 [Axis]
  Suppressed = false
  Type = 0
  expr: Angle = Sketch014.Constraints.angle2
FEATURE [PartDesign::Body] Body011
  AllowCompound = false
  Group = -> [Pad013,Sketch018,Sketch030,Groove004,DatumPlane002,Sketch031,Groove005]
  Origin = -> Origin032
  Tip = -> Groove005
COMPONENT P16 — recipe-attached ("BB1", modeled in this document).
Construction recipe (the document's own serialized feature program — sketch geometry with constraints, then the solid features built on it; lengths are millimeters unless a unit is written):

FEATURE [Sketcher::SketchObject] Sketch019
  ArcFitTolerance = 0
  FullyConstrained = true
  MakeInternals = false
  MapMode = 5
  Placement = pos=(0,0,0) rot=(0.57735,0.57735,0.57735;2.0944rad)
  expr: Constraints[15] = .Constraints.hauteur * 0.1
  expr: Constraints[27] = .Constraints.epaisseur
  sketch-geometry (12):
    g0: LineSegment StartX=-10 StartY=12.5 StartZ=0 EndX=10 EndY=12.5 EndZ=0
    g1: LineSegment StartX=12.5 StartY=10 StartZ=0 EndX=12.5 EndY=-10 EndZ=0
    g2: LineSegment StartX=10 StartY=-12.5 StartZ=0 EndX=-10 EndY=-12.5 EndZ=0
    g3: LineSegment StartX=-12.5 StartY=-10 StartZ=0 EndX=-12.5 EndY=10 EndZ=0
    g4: ArcOfCircle CenterX=-10 CenterY=10 CenterZ=0 NormalX=0 NormalY=0 NormalZ=1 AngleXU=0 Radius=2.5 StartAngle=1.5708 EndAngle=3.14159
    g5: ArcOfCircle CenterX=10 CenterY=10 CenterZ=0 NormalX=0 NormalY=0 NormalZ=1 AngleXU=0 Radius=2.5 StartAngle=2e-16 EndAngle=1.5708
    g6: ArcOfCircle CenterX=10 CenterY=-10 CenterZ=0 NormalX=0 NormalY=0 NormalZ=1 AngleXU=0 Radius=2.5 StartAngle=4.71239 EndAngle=6.28319
    g7: ArcOfCircle CenterX=-10 CenterY=-10 CenterZ=0 NormalX=0 NormalY=0 NormalZ=1 AngleXU=0 Radius=2.5 StartAngle=3.14159 EndAngle=4.71239
    g8: LineSegment StartX=-10.5 StartY=10.5 StartZ=0 EndX=10.5 EndY=10.5 EndZ=0
    g9: LineSegment StartX=10.5 StartY=10.5 StartZ=0 EndX=10.5 EndY=-10.5 EndZ=0
    g10: LineSegment StartX=10.5 StartY=-10.5 StartZ=0 EndX=-10.5 EndY=-10.5 EndZ=0
    g11: LineSegment StartX=-10.5 StartY=-10.5 StartZ=0 EndX=-10.5 EndY=10.5 EndZ=0
  constraints (28):
    c: Horizontal(g2)
    c: Vertical(g3)
    c: Tangent(g0,g4) = 1.5708
    c: Tangent(g3,g4) = 1.5708
    c: Tangent(g0,g5) = 1.5708
    c: Tangent(g1,g5) = 1.5708
    c: Tangent(g1,g6) = 1.5708
    c: Tangent(g2,g6) = 1.5708
    c: Tangent(g2,g7) = 1.5708
    c: Tangent(g3,g7) = 1.5708
    c: Equal(g4,g5)
    c: DistanceY(g2,g0) = 25  'hauteur'
    c: DistanceX(g3,g1) = 25  'largeur'
    c: Equal(g5,g6)
    c: Equal(g6,g7)
    c: Radius(g7) = 2.5
    c: Symmetric(g1,g1,g-1)
    c: Symmetric(g0,g0,g-2)
    c: Coincident(g8,g9)
    c: Coincident(g9,g10)
    c: Coincident(g10,g11)
    c: Coincident(g11,g8)
    c: Horizontal(g10)
    c: Vertical(g11)
    c: Symmetric(g8,g9,g-1)
    c: Symmetric(g8,g8,g-2)
    c: DistanceX(g3,g8) = 2  'epaisseur'
    c: DistanceY(g2,g9) = 2
FEATURE [PartDesign::Pad] Pad014
  Direction = (1,1e-16,-1e-16)
  Length = 685
  Length2 = 100
  Placement = pos=(0,0,0) rot=(0.57735,0.57735,0.57735;2.0944rad)
  Profile = -> Sketch019
  Suppressed = false
  Type = 0
  expr: Length = Spreadsheet.B12 + Spreadsheet.B2 * 3
FEATURE [PartDesign::Body] Body012
  AllowCompound = false
  Group = -> [Sketch019,Pad014]
  Origin = -> Origin034
  Tip = -> Pad014
COMPONENT P17 — recipe-attached ("BB2", modeled in this document).
Construction recipe (the document's own serialized feature program — sketch geometry with constraints, then the solid features built on it; lengths are millimeters unless a unit is written):

FEATURE [Sketcher::SketchObject] Sketch020
  ArcFitTolerance = 0
  FullyConstrained = true
  MakeInternals = false
  MapMode = 5
  Placement = pos=(0,0,0) rot=(0.57735,0.57735,0.57735;2.0944rad)
  expr: Constraints[15] = .Constraints.hauteur * 0.1
  expr: Constraints[27] = .Constraints.epaisseur
  sketch-geometry (12):
    g0: LineSegment StartX=-10 StartY=12.5 StartZ=0 EndX=10 EndY=12.5 EndZ=0
    g1: LineSegment StartX=12.5 StartY=10 StartZ=0 EndX=12.5 EndY=-10 EndZ=0
    g2: LineSegment StartX=10 StartY=-12.5 StartZ=0 EndX=-10 EndY=-12.5 EndZ=0
    g3: LineSegment StartX=-12.5 StartY=-10 StartZ=0 EndX=-12.5 EndY=10 EndZ=0
    g4: ArcOfCircle CenterX=-10 CenterY=10 CenterZ=0 NormalX=0 NormalY=0 NormalZ=1 AngleXU=0 Radius=2.5 StartAngle=1.5708 EndAngle=3.14159
    g5: ArcOfCircle CenterX=10 CenterY=10 CenterZ=0 NormalX=0 NormalY=0 NormalZ=1 AngleXU=0 Radius=2.5 StartAngle=2e-16 EndAngle=1.5708
    g6: ArcOfCircle CenterX=10 CenterY=-10 CenterZ=0 NormalX=0 NormalY=0 NormalZ=1 AngleXU=0 Radius=2.5 StartAngle=4.71239 EndAngle=6.28319
    g7: ArcOfCircle CenterX=-10 CenterY=-10 CenterZ=0 NormalX=0 NormalY=0 NormalZ=1 AngleXU=0 Radius=2.5 StartAngle=3.14159 EndAngle=4.71239
    g8: LineSegment StartX=-10.5 StartY=10.5 StartZ=0 EndX=10.5 EndY=10.5 EndZ=0
    g9: LineSegment StartX=10.5 StartY=10.5 StartZ=0 EndX=10.5 EndY=-10.5 EndZ=0
    g10: LineSegment StartX=10.5 StartY=-10.5 StartZ=0 EndX=-10.5 EndY=-10.5 EndZ=0
    g11: LineSegment StartX=-10.5 StartY=-10.5 StartZ=0 EndX=-10.5 EndY=10.5 EndZ=0
  constraints (28):
    c: Horizontal(g2)
    c: Vertical(g3)
    c: Tangent(g0,g4) = 1.5708
    c: Tangent(g3,g4) = 1.5708
    c: Tangent(g0,g5) = 1.5708
    c: Tangent(g1,g5) = 1.5708
    c: Tangent(g1,g6) = 1.5708
    c: Tangent(g2,g6) = 1.5708
    c: Tangent(g2,g7) = 1.5708
    c: Tangent(g3,g7) = 1.5708
    c: Equal(g4,g5)
    c: DistanceY(g2,g0) = 25  'hauteur'
    c: DistanceX(g3,g1) = 25  'largeur'
    c: Equal(g5,g6)
    c: Equal(g6,g7)
    c: Radius(g7) = 2.5
    c: Symmetric(g1,g1,g-1)
    c: Symmetric(g0,g0,g-2)
    c: Coincident(g8,g9)
    c: Coincident(g9,g10)
    c: Coincident(g10,g11)
    c: Coincident(g11,g8)
    c: Horizontal(g10)
    c: Vertical(g11)
    c: Symmetric(g8,g9,g-1)
    c: Symmetric(g8,g8,g-2)
    c: DistanceX(g3,g8) = 2  'epaisseur'
    c: DistanceY(g2,g9) = 2
FEATURE [PartDesign::Pad] Pad015
  Direction = (1,1e-16,-1e-16)
  Length = 560
  Length2 = 100
  Placement = pos=(0,0,0) rot=(0.57735,0.57735,0.57735;2.0944rad)
  Profile = -> Sketch020
  Suppressed = false
  Type = 0
  expr: Length = Spreadsheet.B12 - Spreadsheet.B2 * 2
FEATURE [PartDesign::Body] Body013
  AllowCompound = false
  Group = -> [Sketch020,Pad015]
  Origin = -> Origin036
  Tip = -> Pad015
COMPONENT P18 — recipe-attached ("BB3", modeled in this document).
Construction recipe (the document's own serialized feature program — sketch geometry with constraints, then the solid features built on it; lengths are millimeters unless a unit is written):

FEATURE [Sketcher::SketchObject] Sketch021
  ArcFitTolerance = 0
  FullyConstrained = true
  MakeInternals = false
  MapMode = 5
  Placement = pos=(0,0,0) rot=(0.57735,0.57735,0.57735;2.0944rad)
  expr: Constraints[15] = .Constraints.hauteur * 0.1
  expr: Constraints[27] = .Constraints.epaisseur
  sketch-geometry (12):
    g0: LineSegment StartX=-10 StartY=12.5 StartZ=0 EndX=10 EndY=12.5 EndZ=0
    g1: LineSegment StartX=12.5 StartY=10 StartZ=0 EndX=12.5 EndY=-10 EndZ=0
    g2: LineSegment StartX=10 StartY=-12.5 StartZ=0 EndX=-10 EndY=-12.5 EndZ=0
    g3: LineSegment StartX=-12.5 StartY=-10 StartZ=0 EndX=-12.5 EndY=10 EndZ=0
    g4: ArcOfCircle CenterX=-10 CenterY=10 CenterZ=0 NormalX=0 NormalY=0 NormalZ=1 AngleXU=0 Radius=2.5 StartAngle=1.5708 EndAngle=3.14159
    g5: ArcOfCircle CenterX=10 CenterY=10 CenterZ=0 NormalX=0 NormalY=0 NormalZ=1 AngleXU=0 Radius=2.5 StartAngle=2e-16 EndAngle=1.5708
    g6: ArcOfCircle CenterX=10 CenterY=-10 CenterZ=0 NormalX=0 NormalY=0 NormalZ=1 AngleXU=0 Radius=2.5 StartAngle=4.71239 EndAngle=6.28319
    g7: ArcOfCircle CenterX=-10 CenterY=-10 CenterZ=0 NormalX=0 NormalY=0 NormalZ=1 AngleXU=0 Radius=2.5 StartAngle=3.14159 EndAngle=4.71239
    g8: LineSegment StartX=-10.5 StartY=10.5 StartZ=0 EndX=10.5 EndY=10.5 EndZ=0
    g9: LineSegment StartX=10.5 StartY=10.5 StartZ=0 EndX=10.5 EndY=-10.5 EndZ=0
    g10: LineSegment StartX=10.5 StartY=-10.5 StartZ=0 EndX=-10.5 EndY=-10.5 EndZ=0
    g11: LineSegment StartX=-10.5 StartY=-10.5 StartZ=0 EndX=-10.5 EndY=10.5 EndZ=0
  constraints (28):
    c: Horizontal(g2)
    c: Vertical(g3)
    c: Tangent(g0,g4) = 1.5708
    c: Tangent(g3,g4) = 1.5708
    c: Tangent(g0,g5) = 1.5708
    c: Tangent(g1,g5) = 1.5708
    c: Tangent(g1,g6) = 1.5708
    c: Tangent(g2,g6) = 1.5708
    c: Tangent(g2,g7) = 1.5708
    c: Tangent(g3,g7) = 1.5708
    c: Equal(g4,g5)
    c: DistanceY(g2,g0) = 25  'hauteur'
    c: DistanceX(g3,g1) = 25  'largeur'
    c: Equal(g5,g6)
    c: Equal(g6,g7)
    c: Radius(g7) = 2.5
    c: Symmetric(g1,g1,g-1)
    c: Symmetric(g0,g0,g-2)
    c: Coincident(g8,g9)
    c: Coincident(g9,g10)
    c: Coincident(g10,g11)
    c: Coincident(g11,g8)
    c: Horizontal(g10)
    c: Vertical(g11)
    c: Symmetric(g8,g9,g-1)
    c: Symmetric(g8,g8,g-2)
    c: DistanceX(g3,g8) = 2  'epaisseur'
    c: DistanceY(g2,g9) = 2
FEATURE [PartDesign::Pad] Pad016
  Direction = (1,1e-16,-1e-16)
  Length = 610
  Length2 = 100
  Placement = pos=(0,0,0) rot=(0.57735,0.57735,0.57735;2.0944rad)
  Profile = -> Sketch021
  Suppressed = false
  Type = 0
  expr: Length = Spreadsheet.D4
FEATURE [PartDesign::Body] Body014
  AllowCompound = false
  Group = -> [Sketch021,Pad016]
  Origin = -> Origin038
  Tip = -> Pad016
COMPONENT P19 — recipe-attached ("A16", modeled in this document).
Construction recipe (the document's own serialized feature program — sketch geometry with constraints, then the solid features built on it; lengths are millimeters unless a unit is written):

FEATURE [Sketcher::SketchObject] Sketch022
  ArcFitTolerance = 0
  FullyConstrained = true
  MakeInternals = false
  MapMode = 5
  Placement = pos=(0,0,0) rot=(0.57735,0.57735,0.57735;2.0944rad)
  expr: Constraints[15] = .Constraints.hauteur * 0.1
  expr: Constraints[27] = .Constraints.epaisseur
  sketch-geometry (12):
    g0: LineSegment StartX=-12 StartY=15 StartZ=0 EndX=12 EndY=15 EndZ=0
    g1: LineSegment StartX=15 StartY=12 StartZ=0 EndX=15 EndY=-12 EndZ=0
    g2: LineSegment StartX=12 StartY=-15 StartZ=0 EndX=-12 EndY=-15 EndZ=0
    g3: LineSegment StartX=-15 StartY=-12 StartZ=0 EndX=-15 EndY=12 EndZ=0
    g4: ArcOfCircle CenterX=-12 CenterY=12 CenterZ=0 NormalX=0 NormalY=0 NormalZ=1 AngleXU=0 Radius=3 StartAngle=1.5708 EndAngle=3.14159
    g5: ArcOfCircle CenterX=12 CenterY=12 CenterZ=0 NormalX=0 NormalY=0 NormalZ=1 AngleXU=0 Radius=3 StartAngle=1e-16 EndAngle=1.5708
    g6: ArcOfCircle CenterX=12 CenterY=-12 CenterZ=0 NormalX=0 NormalY=0 NormalZ=1 AngleXU=0 Radius=3 StartAngle=4.71239 EndAngle=6.28319
    g7: ArcOfCircle CenterX=-12 CenterY=-12 CenterZ=0 NormalX=0 NormalY=0 NormalZ=1 AngleXU=0 Radius=3 StartAngle=3.14159 EndAngle=4.71239
    g8: LineSegment StartX=-13 StartY=13 StartZ=0 EndX=13 EndY=13 EndZ=0
    g9: LineSegment StartX=13 StartY=13 StartZ=0 EndX=13 EndY=-13 EndZ=0
    g10: LineSegment StartX=13 StartY=-13 StartZ=0 EndX=-13 EndY=-13 EndZ=0
    g11: LineSegment StartX=-13 StartY=-13 StartZ=0 EndX=-13 EndY=13 EndZ=0
  constraints (28):
    c: Horizontal(g2)
    c: Vertical(g3)
    c: Tangent(g0,g4) = 1.5708
    c: Tangent(g3,g4) = 1.5708
    c: Tangent(g0,g5) = 1.5708
    c: Tangent(g1,g5) = 1.5708
    c: Tangent(g1,g6) = 1.5708
    c: Tangent(g2,g6) = 1.5708
    c: Tangent(g2,g7) = 1.5708
    c: Tangent(g3,g7) = 1.5708
    c: Equal(g4,g5)
    c: DistanceY(g2,g0) = 30  'hauteur'
    c: DistanceX(g3,g1) = 30  'largeur'
    c: Equal(g5,g6)
    c: Equal(g6,g7)
    c: Radius(g7) = 3
    c: Symmetric(g1,g1,g-1)
    c: Symmetric(g0,g0,g-2)
    c: Coincident(g8,g9)
    c: Coincident(g9,g10)
    c: Coincident(g10,g11)
    c: Coincident(g11,g8)
    c: Horizontal(g10)
    c: Vertical(g11)
    c: Symmetric(g8,g9,g-1)
    c: Symmetric(g8,g8,g-2)
    c: DistanceX(g3,g8) = 2  'epaisseur'
    c: DistanceY(g2,g9) = 2
FEATURE [PartDesign::Pad] Pad017
  Direction = (1,1e-16,-1e-16)
  Length = 50
  Length2 = 100
  Placement = pos=(0,0,0) rot=(0.57735,0.57735,0.57735;2.0944rad)
  Profile = -> Sketch022
  Suppressed = false
  Type = 0
  expr: Length = 2 * Spreadsheet.B2
FEATURE [PartDesign::Body] Body015
  AllowCompound = false
  Group = -> [Sketch022,Pad017]
  Origin = -> Origin040
  Tip = -> Pad017
COMPONENT P20 — recipe-attached ("A17", modeled in this document).
Construction recipe (the document's own serialized feature program — sketch geometry with constraints, then the solid features built on it; lengths are millimeters unless a unit is written):

FEATURE [Sketcher::SketchObject] Sketch024
  ArcFitTolerance = 0
  AttachmentSupport = -> [XZ_Plane042]
  FullyConstrained = true
  MakeInternals = false
  MapMode = 5
  Placement = pos=(0,0,0) rot=(1,0,0;1.5708rad)
  expr: .Constraints.diametre = Spreadsheet.B13
  sketch-geometry (4):
    g0: Circle CenterX=0 CenterY=0 CenterZ=0 NormalX=0 NormalY=0 NormalZ=1 AngleXU=0 Radius=13
    g1: Circle CenterX=0 CenterY=0 CenterZ=0 NormalX=0 NormalY=0 NormalZ=1 AngleXU=0 Radius=15
    g2: GeomPoint [constr] X=-15 Y=0 Z=0
    g3: GeomPoint [constr] X=-13 Y=0 Z=0
  constraints (8):
    c: Coincident(g1,g0)
    c: PointOnObject(g2,g1)
    c: PointOnObject(g3,g0)
    c: Coincident(g0,g-1)
    c: PointOnObject(g3,g-1)
    c: PointOnObject(g2,g-1)
    c: DistanceX(g2,g3) = 2  'epaisseur'
    c: Diameter(g1) = 30  'diametre'
FEATURE [PartDesign::Pad] Pad018
  Direction = (0,-1,2e-16)
  Length = 300
  Length2 = 100
  Placement = pos=(0,0,0) rot=(1,0,0;1.5708rad)
  Profile = -> Sketch024
  Suppressed = false
  Type = 0
FEATURE [PartDesign::Body] Body016
  AllowCompound = false
  Group = -> [Sketch024,Pad018]
  Origin = -> Origin042
  Tip = -> Pad018
COMPONENT P21 — recipe-attached ("A18", modeled in this document).
Construction recipe (the document's own serialized feature program — sketch geometry with constraints, then the solid features built on it; lengths are millimeters unless a unit is written):

FEATURE [Sketcher::SketchObject] Sketch025
  ArcFitTolerance = 0
  FullyConstrained = true
  MakeInternals = false
  MapMode = 5
  Placement = pos=(0,0,0) rot=(0.57735,0.57735,0.57735;2.0944rad)
  expr: Constraints[15] = .Constraints.hauteur * 0.1
  expr: Constraints[27] = .Constraints.epaisseur
  sketch-geometry (12):
    g0: LineSegment StartX=-10 StartY=12.5 StartZ=0 EndX=10 EndY=12.5 EndZ=0
    g1: LineSegment StartX=12.5 StartY=10 StartZ=0 EndX=12.5 EndY=-10 EndZ=0
    g2: LineSegment StartX=10 StartY=-12.5 StartZ=0 EndX=-10 EndY=-12.5 EndZ=0
    g3: LineSegment StartX=-12.5 StartY=-10 StartZ=0 EndX=-12.5 EndY=10 EndZ=0
    g4: ArcOfCircle CenterX=-10 CenterY=10 CenterZ=0 NormalX=0 NormalY=0 NormalZ=1 AngleXU=0 Radius=2.5 StartAngle=1.5708 EndAngle=3.14159
    g5: ArcOfCircle CenterX=10 CenterY=10 CenterZ=0 NormalX=0 NormalY=0 NormalZ=1 AngleXU=0 Radius=2.5 StartAngle=2e-16 EndAngle=1.5708
    g6: ArcOfCircle CenterX=10 CenterY=-10 CenterZ=0 NormalX=0 NormalY=0 NormalZ=1 AngleXU=0 Radius=2.5 StartAngle=4.71239 EndAngle=6.28319
    g7: ArcOfCircle CenterX=-10 CenterY=-10 CenterZ=0 NormalX=0 NormalY=0 NormalZ=1 AngleXU=0 Radius=2.5 StartAngle=3.14159 EndAngle=4.71239
    g8: LineSegment StartX=-10.5 StartY=10.5 StartZ=0 EndX=10.5 EndY=10.5 EndZ=0
    g9: LineSegment StartX=10.5 StartY=10.5 StartZ=0 EndX=10.5 EndY=-10.5 EndZ=0
    g10: LineSegment StartX=10.5 StartY=-10.5 StartZ=0 EndX=-10.5 EndY=-10.5 EndZ=0
    g11: LineSegment StartX=-10.5 StartY=-10.5 StartZ=0 EndX=-10.5 EndY=10.5 EndZ=0
  constraints (28):
    c: Horizontal(g2)
    c: Vertical(g3)
    c: Tangent(g0,g4) = 1.5708
    c: Tangent(g3,g4) = 1.5708
    c: Tangent(g0,g5) = 1.5708
    c: Tangent(g1,g5) = 1.5708
    c: Tangent(g1,g6) = 1.5708
    c: Tangent(g2,g6) = 1.5708
    c: Tangent(g2,g7) = 1.5708
    c: Tangent(g3,g7) = 1.5708
    c: Equal(g4,g5)
    c: DistanceY(g2,g0) = 25  'hauteur'
    c: DistanceX(g3,g1) = 25  'largeur'
    c: Equal(g5,g6)
    c: Equal(g6,g7)
    c: Radius(g7) = 2.5
    c: Symmetric(g1,g1,g-1)
    c: Symmetric(g0,g0,g-2)
    c: Coincident(g8,g9)
    c: Coincident(g9,g10)
    c: Coincident(g10,g11)
    c: Coincident(g11,g8)
    c: Horizontal(g10)
    c: Vertical(g11)
    c: Symmetric(g8,g9,g-1)
    c: Symmetric(g8,g8,g-2)
    c: DistanceX(g3,g8) = 2  'epaisseur'
    c: DistanceY(g2,g9) = 2
FEATURE [PartDesign::Pad] Pad019
  Direction = (1,1e-16,-1e-16)
  Length = 142
  Length2 = 100
  Placement = pos=(0,0,0) rot=(0.57735,0.57735,0.57735;2.0944rad)
  Profile = -> Sketch025
  Suppressed = false
  Type = 0
FEATURE [Sketcher::SketchObject] Sketch026
  ArcFitTolerance = 1e-06
  AttachmentSupport = -> [YZ_Plane044]
  ExternalGeometry = -> [Pad019]
  FullyConstrained = false
  MakeInternals = false
  MapMode = 5
  Placement = pos=(0,0,0) rot=(0.57735,0.57735,0.57735;2.0944rad)
  sketch-geometry (5):
    g0: LineSegment [constr] StartX=-12.5 StartY=34.6544 StartZ=0 EndX=-12.5 EndY=-40.7923 EndZ=0
    g1: LineSegment StartX=-12.5 StartY=-17.5 StartZ=0 EndX=57.5 EndY=-17.5 EndZ=0
    g2: LineSegment StartX=57.5 StartY=-17.5 StartZ=0 EndX=57.5 EndY=17.5 EndZ=0
    g3: LineSegment StartX=57.5 StartY=17.5 StartZ=0 EndX=-12.5 EndY=17.5 EndZ=0
    g4: LineSegment StartX=-12.5 StartY=17.5 StartZ=0 EndX=-12.5 EndY=-17.5 EndZ=0
  constraints (13):
    c: Coincident(g1,g2)
    c: Coincident(g2,g3)
    c: Coincident(g3,g4)
    c: Coincident(g4,g1)
    c: Horizontal(g3)
    c: Vertical(g2)
    c: Distance(g2,g4) = 70
    c: Distance(g1,g3) = 35
    c: Vertical(g0)
    c: PointOnObject(g-3,g0)
    c: Symmetric(g3,g1,g-1)
    c: PointOnObject(g3,g0)
    c: Horizontal(g1)
FEATURE [PartDesign::Plane] DatumPlane
  AttachmentSupport = -> [Pad019]
  Length = 60
  MapMode = 5
  Placement = pos=(142,6.25e-14,0) rot=(0.57735,0.57735,0.57735;2.0944rad)
  ResizeMode = 0
  Width = 60
FEATURE [Sketcher::SketchObject] Sketch027
  ArcFitTolerance = 1e-06
  AttachmentSupport = -> [DatumPlane]
  ExternalGeometry = -> [Pad019]
  FullyConstrained = false
  MakeInternals = false
  MapMode = 5
  Placement = pos=(142,6.25e-14,0) rot=(0.57735,0.57735,0.57735;2.0944rad)
  sketch-geometry (5):
    g0: LineSegment [constr] StartX=-12.5 StartY=-38.9997 StartZ=0 EndX=-12.5 EndY=36.6406 EndZ=0
    g1: LineSegment StartX=-12.5 StartY=-17.5 StartZ=0 EndX=57.5 EndY=-17.5 EndZ=0
    g2: LineSegment StartX=57.5 StartY=-17.5 StartZ=0 EndX=57.5 EndY=17.5 EndZ=0
    g3: LineSegment StartX=57.5 StartY=17.5 StartZ=0 EndX=-12.5 EndY=17.5 EndZ=0
    g4: LineSegment StartX=-12.5 StartY=17.5 StartZ=0 EndX=-12.5 EndY=-17.5 EndZ=0
  constraints (13):
    c: Coincident(g1,g2)
    c: Coincident(g2,g3)
    c: Coincident(g3,g4)
    c: Coincident(g4,g1)
    c: Horizontal(g3)
    c: Vertical(g2)
    c: Distance(g2,g4) = 70
    c: Distance(g1,g3) = 35
    c: PointOnObject(g0,g-4)
    c: Vertical(g0)
    c: Symmetric(g3,g1,g-1)
    c: Horizontal(g1)
    c: PointOnObject(g1,g0)
FEATURE [PartDesign::Groove] Groove
  Angle = 45
  Angle2 = 60
  Axis = (0,0,-75.4468)
  Base = (0,-12.5,34.6544)
  BaseFeature = -> Pad019
  Placement = pos=(0,0,0) rot=(0.57735,0.57735,0.57735;2.0944rad)
  Profile = -> Sketch026
  ReferenceAxis = -> Sketch026 [Axis]
  Suppressed = false
  Type = 0
FEATURE [PartDesign::Groove] Groove001
  Angle = 45
  Angle2 = 60
  Axis = (0,0,75.6403)
  Base = (142,-12.5,-38.9997)
  BaseFeature = -> Groove
  Placement = pos=(0,0,0) rot=(0.57735,0.57735,0.57735;2.0944rad)
  Profile = -> Sketch027
  ReferenceAxis = -> Sketch027 [Axis]
  Suppressed = false
  Type = 0
FEATURE [PartDesign::Body] Body017
  AllowCompound = false
  Group = -> [Sketch025,Pad019,Sketch026,DatumPlane,Sketch027,Groove,Groove001]
  Origin = -> Origin044
  Tip = -> Groove001
COMPONENT P22 — recipe-attached ("Roue_increvable___389___axe25_L_82", modeled in this document).
Construction recipe (the document's own serialized feature program — sketch geometry with constraints, then the solid features built on it; lengths are millimeters unless a unit is written):

FEATURE [Sketcher::SketchObject] Sketch005
  ArcFitTolerance = 0
  AttachmentSupport = -> [XY_Plane010]
  FullyConstrained = true
  MakeInternals = false
  MapMode = 5
  sketch-geometry (16):
    g0: LineSegment StartX=-41 StartY=12.5 StartZ=0 EndX=41 EndY=12.5 EndZ=0
    g1: LineSegment StartX=-41 StartY=12.5 StartZ=0 EndX=-41 EndY=17.5 EndZ=0
    g2: LineSegment StartX=-41 StartY=17.5 StartZ=0 EndX=-38 EndY=17.5 EndZ=0
    g3: LineSegment StartX=-38 StartY=17.5 StartZ=0 EndX=-38 EndY=120 EndZ=0
    g4: LineSegment StartX=-38 StartY=120 StartZ=0 EndX=-36 EndY=120 EndZ=0
    g5: LineSegment StartX=-36 StartY=120 StartZ=0 EndX=-36 EndY=122 EndZ=0
    g6: LineSegment StartX=-36 StartY=122 StartZ=0 EndX=-38 EndY=122 EndZ=0
    g7: LineSegment StartX=41 StartY=12.5 StartZ=0 EndX=41 EndY=17.5 EndZ=0
    g8: LineSegment StartX=41 StartY=17.5 StartZ=0 EndX=38 EndY=17.5 EndZ=0
    g9: LineSegment StartX=38 StartY=17.5 StartZ=0 EndX=38 EndY=120 EndZ=0
    g10: LineSegment StartX=38 StartY=120 StartZ=0 EndX=36 EndY=120 EndZ=0
    g11: LineSegment StartX=36 StartY=120 StartZ=0 EndX=36 EndY=122 EndZ=0
    g12: LineSegment StartX=36 StartY=122 StartZ=0 EndX=38 EndY=122 EndZ=0
    g13: GeomPoint [constr] X=-1e-15 Y=151.744 Z=0
    g14: GeomPoint [constr] X=0 Y=200 Z=0
    g15: ArcOfCircle CenterX=-1e-15 CenterY=151.744 CenterZ=0 NormalX=0 NormalY=0 NormalZ=1 AngleXU=0 Radius=48.2564 StartAngle=5.61907 EndAngle=10.0889
  constraints (42):
    c: Symmetric(g0,g0,g-2)
    c: Coincident(g0,g1)
    c: Vertical(g1)
    c: Coincident(g1,g2)
    c: Horizontal(g2)
    c: Coincident(g2,g3)
    c: Vertical(g3)
    c: Coincident(g3,g4)
    c: Horizontal(g4)
    c: Coincident(g4,g5)
    c: Coincident(g5,g6)
    c: Horizontal(g6)
    c: Vertical(g5)
    c: PointOnObject(g6,g3)
    c: DistanceX(g2,g2) = 3
    c: DistanceX(g4,g4) = 2
    c: DistanceY(g5,g5) = 2
    c: Vertical(g7)
    c: Coincident(g7,g8)
    c: Horizontal(g8)
    c: Coincident(g8,g9)
    c: Coincident(g9,g10)
    c: Horizontal(g10)
    c: Coincident(g10,g11)
    c: Coincident(g11,g12)
    c: Horizontal(g12)
    c: Vertical(g11)
    c: PointOnObject(g12,g9)
    c: Symmetric(g9,g3,g-2)
    c: Symmetric(g5,g11,g-2)
    c: DistanceX(g2,g8) = 76
    c: Coincident(g0,g7)
    c: DistanceY(g-1,g0) = 12.5
    c: DistanceY(g7,g7) = 5
    c: Symmetric(g2,g8,g-2)
    c: PointOnObject(g14,g-2)
    c: DistanceY(g-1,g9) = 120
    c: DistanceY(g-1,g14) = 200
    c: Coincident(g15,g13)
    c: Coincident(g15,g6)
    c: Coincident(g15,g12)
    c: PointOnObject(g14,g15)
FEATURE [PartDesign::Revolution] Revolution
  Angle = 360
  Angle2 = 60
  Axis = (1,0,0)
  Base = (0,0,0)
  Profile = -> Sketch005
  ReferenceAxis = -> Sketch005 [H_Axis]
  Suppressed = false
  Type = 0
FEATURE [PartDesign::Body] Body004
  AllowCompound = false
  Group = -> [Sketch005,Revolution]
  Origin = -> Origin010
  Tip = -> Revolution
COMPONENT P23 — recipe-attached ("goupille elastique 5 x 80", modeled in this document).
Construction recipe (the document's own serialized feature program — sketch geometry with constraints, then the solid features built on it; lengths are millimeters unless a unit is written):

FEATURE [PartDesign::CoordinateSystem] LCS_Origin004
  AttacherType = Attacher::AttachEngine3D
  AttachmentSupport = -> [X_Axis050]
  MapMode = 2
FEATURE [Sketcher::SketchObject] Sketch036
  ArcFitTolerance = 1e-06
  AttachmentSupport = -> [XZ_Plane048]
  FullyConstrained = false
  MakeInternals = false
  MapMode = 5
  Placement = pos=(0,0,0) rot=(1,0,0;1.5708rad)
  sketch-geometry (11):
    g0: Circle [constr] CenterX=0 CenterY=0 CenterZ=0 NormalX=0 NormalY=0 NormalZ=1 AngleXU=0 Radius=13.75
    g1: LineSegment [constr] StartX=0 StartY=-40 StartZ=0 EndX=0 EndY=40 EndZ=0
    g2: Circle [constr] CenterX=-10 CenterY=30 CenterZ=0 NormalX=0 NormalY=0 NormalZ=1 AngleXU=0 Radius=10
    g3: GeomPoint [constr] X=0 Y=30 Z=0
    g4: LineSegment [constr] StartX=0 StartY=40 StartZ=0 EndX=-69.1627 EndY=40 EndZ=0
    g5: LineSegment StartX=0 StartY=-40 StartZ=0 EndX=0 EndY=30 EndZ=0
    g6: ArcOfCircle CenterX=-10 CenterY=30 CenterZ=0 NormalX=0 NormalY=0 NormalZ=1 AngleXU=0 Radius=10 StartAngle=4.06135e-09 EndAngle=4.58938
    g7: ArcOfCircle CenterX=-11.8728 CenterY=14.8514 CenterZ=0 NormalX=0 NormalY=0 NormalZ=1 AngleXU=0 Radius=5.26396 StartAngle=5.38202 EndAngle=7.73097
    g8: ArcOfCircle CenterX=0 CenterY=0 CenterZ=0 NormalX=0 NormalY=0 NormalZ=1 AngleXU=0 Radius=13.75 StartAngle=2.24702 EndAngle=4.04719
    g9: ArcOfCircle CenterX=-12.0115 CenterY=-15.2346 CenterZ=0 NormalX=0 NormalY=0 NormalZ=1 AngleXU=0 Radius=5.65039 StartAngle=5.15136 EndAngle=7.18037
    g10: LineSegment StartX=-9.61003 StartY=-20.3493 StartZ=0 EndX=-12.9682 EndY=-21.926 EndZ=0
  constraints (21):
    c: Diameter(g0) = 27.5
    c: Coincident(g0,g-1)
    c: Distance(g1) = 80
    c: Vertical(g1)
    c: Diameter(g2) = 20
    c: PointOnObject(g3,g2)
    c: PointOnObject(g3,g1)
    c: Coincident(g4,g1)
    c: Horizontal(g4)
    c: Tangent(g4,g2)
    c: Symmetric(g1,g1,g0)
    c: Coincident(g5,g1)
    c: Coincident(g5,g3)
    c: Coincident(g6,g2)
    c: Coincident(g6,g3)
    c: PointOnObject(g7,g0)
    c: Coincident(g7,g6)
    c: Coincident(g8,g0)
    c: Coincident(g8,g7)
    c: Coincident(g9,g8)
    c: Tangent(g10,g9) = 1.5708
FEATURE [PartDesign::Plane] DatumPlane005
  AttachmentSupport = -> [Sketch036]
  Length = 60
  MapMode = 7
  Placement = pos=(0,-8.9e-15,-40) rot=(0,1,0;3.14159rad)
  ResizeMode = 0
  Width = 60
FEATURE [Sketcher::SketchObject] Sketch037
  ArcFitTolerance = 1e-06
  AttachmentSupport = -> [DatumPlane005]
  FullyConstrained = true
  MakeInternals = false
  MapMode = 5
  Placement = pos=(0,-8.9e-15,-40) rot=(0,1,0;3.14159rad)
  sketch-geometry (1):
    g0: Circle CenterX=0 CenterY=0 CenterZ=0 NormalX=0 NormalY=0 NormalZ=1 AngleXU=0 Radius=2.5
  constraints (2):
    c: Diameter(g0) = 5
    c: Coincident(g0,g-1)
FEATURE [PartDesign::AdditivePipe] AdditivePipe001
  AuxilleryCurvelinear = true
  AuxillerySpineTangent = false
  Binormal = (0,0,0)
  Mode = 0
  Placement = pos=(0,-8.9e-15,-40) rot=(0,1,0;3.14159rad)
  Profile = -> Sketch037
  Spine = -> Sketch036
  SpineTangent = false
  Suppressed = false
  Transformation = 0
  Transition = 0
FEATURE [PartDesign::Body] goupille
  AllowCompound = false
  Group = -> [LCS_Origin004,Sketch036,DatumPlane005,Sketch037,AdditivePipe001]
  Origin = -> Origin048
  Tip = -> AdditivePipe001
COMPONENT P24 — recipe-attached ("rondelle 25", modeled in this document).
Construction recipe (the document's own serialized feature program — sketch geometry with constraints, then the solid features built on it; lengths are millimeters unless a unit is written):

FEATURE [PartDesign::CoordinateSystem] LCS_Origin002
  AttacherType = Attacher::AttachEngine3D
  AttachmentSupport = -> [X_Axis048]
  MapMode = 2
FEATURE [Sketcher::SketchObject] Sketch035
  ArcFitTolerance = 1e-06
  AttachmentSupport = -> [YZ_Plane046]
  FullyConstrained = true
  MakeInternals = false
  MapMode = 5
  Placement = pos=(0,0,0) rot=(0.57735,0.57735,0.57735;2.0944rad)
  sketch-geometry (4):
    g0: LineSegment StartX=-1 StartY=28 StartZ=0 EndX=-1 EndY=13 EndZ=0
    g1: LineSegment StartX=-1 StartY=13 StartZ=0 EndX=1 EndY=13 EndZ=0
    g2: LineSegment StartX=1 StartY=13 StartZ=0 EndX=1 EndY=28 EndZ=0
    g3: LineSegment StartX=1 StartY=28 StartZ=0 EndX=-1 EndY=28 EndZ=0
  constraints (11):
    c: Coincident(g0,g1)
    c: Coincident(g1,g2)
    c: Coincident(g2,g3)
    c: Coincident(g3,g0)
    c: Vertical(g0)
    c: Vertical(g2)
    c: Horizontal(g3)
    c: Symmetric(g0,g1,g-2)
    c: DistanceY(g-1,g1) = 13  'rayint'
    c: DistanceY(g-1,g2) = 28  'rayext'
    c: DistanceX(g3,g3) = 2  'ep'
FEATURE [PartDesign::Revolution] Revolution001
  Angle = 360
  Angle2 = 60
  Axis = (0,1,0)
  Base = (0,0,0)
  Placement = pos=(0,0,0) rot=(1,1,1;2.0944rad)
  Profile = -> Sketch035
  ReferenceAxis = -> Sketch035 [H_Axis]
  Suppressed = false
  Type = 0
FEATURE [PartDesign::Body] rondellle
  AllowCompound = false
  Group = -> [LCS_Origin002,Sketch035,Revolution001]
  Origin = -> Origin046
  Tip = -> Revolution001
PROVENANCE & LICENSES
A FreeCAD (.FCStd) document from a public repository crawl; recipes are the document's own serialized feature recipes (and, for linked parts, companion documents' recipes).
License: gpl-3.0.
